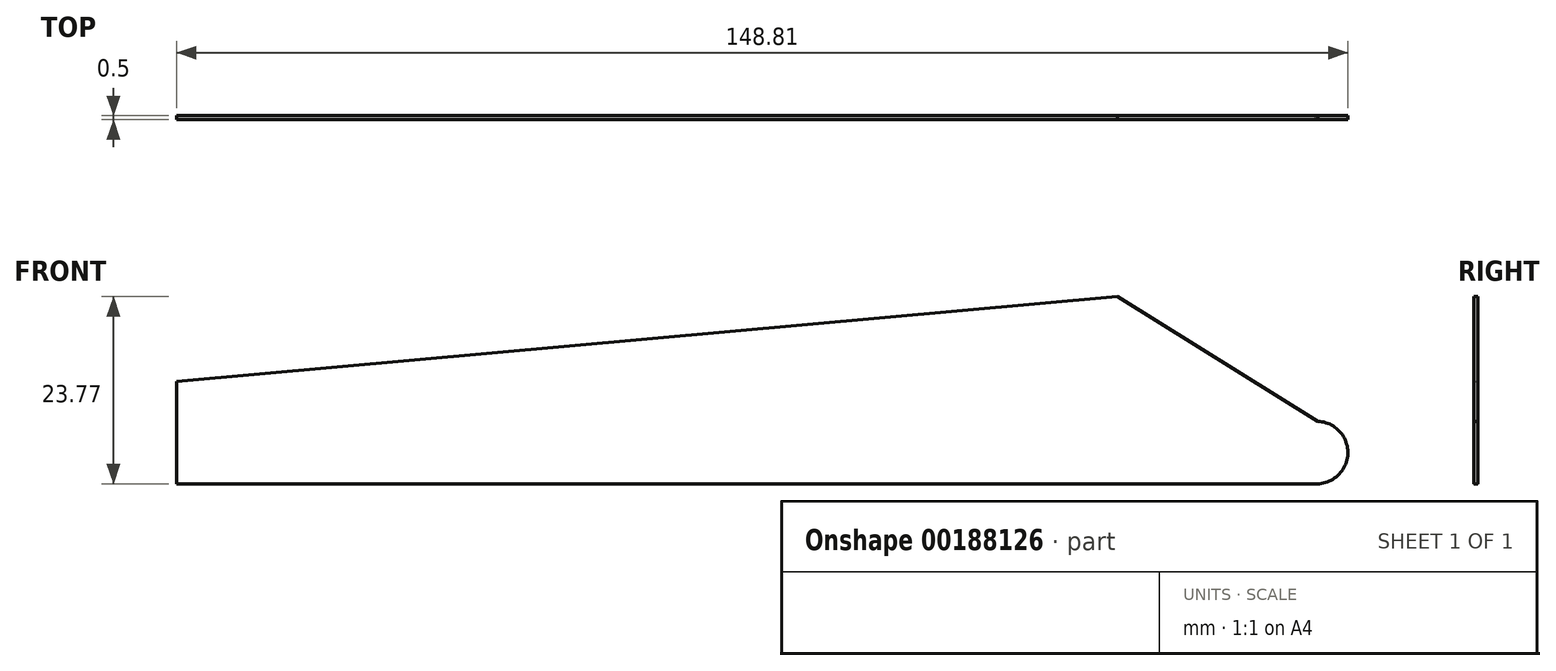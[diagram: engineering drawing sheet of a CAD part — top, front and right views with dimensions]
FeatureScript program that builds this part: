
annotation { "Feature Type Name" : "Feature", "Feature Type Description" : "" }
export const myFeature = defineFeature(function(context is Context, id is Id, definition is map)
    precondition{}
    {
        {
            var Q0;
            Q0=qCreatedBy(makeId("Front.planeOp"),FACE);
            var sketch = newSketch(context, id + "F0", { "sketchPlane" : qUnion([Q0])});
            skLineSegment(sketch, "E0", {"start": v(74.3, 0) * mm, "end": v(-70.7, 0) * mm});
            skLineSegment(sketch, "E1", {"start": v(-70.7, 0) * mm, "end": v(-70.7, 13) * mm});
            skLineSegment(sketch, "E2", {"start": v(-70.7, 13) * mm, "end": v(48.82, 23.77) * mm});
            skLineSegment(sketch, "E3", {"start": v(48.82, 23.77) * mm, "end": v(74.3, 7.94) * mm});
            skCircle(sketch, "E4", {"center": v(74.14, 3.97) * mm, "radius": 3.98 * mm});
            skPoint(sketch, "E4.third.point", {"position": v(70.4, 2.62) * mm});
            skSolve(sketch);
        }
        {
            var Q0;
            Q0 = qSketchRegion(id + "F0", true);
            extrude(context, id + "F1", {"entities" : qUnion([Q0]), "depth" : .5 * mm});
        }
    });
